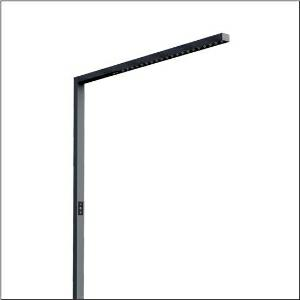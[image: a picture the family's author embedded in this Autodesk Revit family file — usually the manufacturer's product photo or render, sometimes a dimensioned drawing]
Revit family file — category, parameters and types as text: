
# Revit family: silica_r__31_floor_51my52fatcb_ab5c
name_source: partatom
category: Lighting Fixtures
units: mm (PartAtom-declared; Revit-internal decimal feet)

## family parameters
Cut with Voids When Loaded = No
Host = Face
Light Source = No
Part Type = Normal
Room Calculation Point = No
Round Connector Dimension = Use Diameter
Shared = No

## types (1)
- --- (1 x LED, 8520 lm, 71 W, 4000K)
    Apparent Load = 71 VA
    CIE Flux Codes = 86 100 100 24 100
    Color Rendering = 80
    Color Temperature = 4000K
    Default Elevation = 1800 mm
    Description = Silica® 31 Floor, floorstanding luminaire, secondary optical cover: cover panel, of PMMA, light emission: direct/indirect distribution, primary light characteristic: symmetric, installation type: not mounted, LED, rated luminous flux: 8.520lm, luminous efficacy: 120lm/W, light colour: 8tw, colour temperature: 2700..6500K, control gear: Touchdim, daylight-dependent control, with cable with plug, mains connection: 230V, AC, 50Hz, connection cable pre-assembled, rated input power: 71W, luminaire head, of aluminium, jet black (RAL 9005), length: 1.203mm, width: 52mm, supporting column, angular, of aluminium, jet black (RAL 9005), baseplate, of steel, jet black (RAL 9005), protection rating (complete): IP20, insulation class (complete): insulation class I (protective earthing), certification: CE, permissible operating ambient temperature: -20..+40°C, standard: EN 50419, packaging unit: 1 piece
    Height = 36 mm
    Lamp = 1 x LED
    Lamp Light Flux = 8520 lm
    Lamp Power = 71 W
    Lamp count = 1
    Length = 1203 mm
    Luminous efficacy = 120 lm/W
    Manufacturer = Siteco
    ModVariant = No
    Model = 51MY52FATCB
    Mounting Place = Floor
    Mounting Type = Freestanding
    Number of Poles = 1
    OnlyDefault = Yes
    Power Factor = 1
    Product Name = Silica® 31 Floor
    Product group = floorstanding luminaire
    ProductGroupID = 1302
    Protection Class = Protection class I
    Protection Degree = IP 20
    RLX_Detail_Level = 1
    RLX_Emergency_Light_Flux = 0 lm
    RLX_Emergency_Type = 0
    RLX_Emergency_Type_DB = No
    RlxData = <blob elided: 20101 chars, md5=1a1666dd>
    Socket = socket
    Standby Power = 0 W
    System Light Flux = 8520 lm
    System Power = 71 W
    Type Comments = factory setting
    Type Image = l_1275297.jpg
    URL = http://relux.com
    VarID = @adj_080226
    Voltage = 0 V
    Weight = 0.00 kg
    Width = 52 mm  [stored 0.170604 ft]

note: [stored X ft] marks values corroborated as IEEE doubles in the binary element streams (Revit-internal decimal feet)

## geometry (parser evidence)
native form markers: Blend x4, Sweep x16
no freeform markers — native parametric forms only
